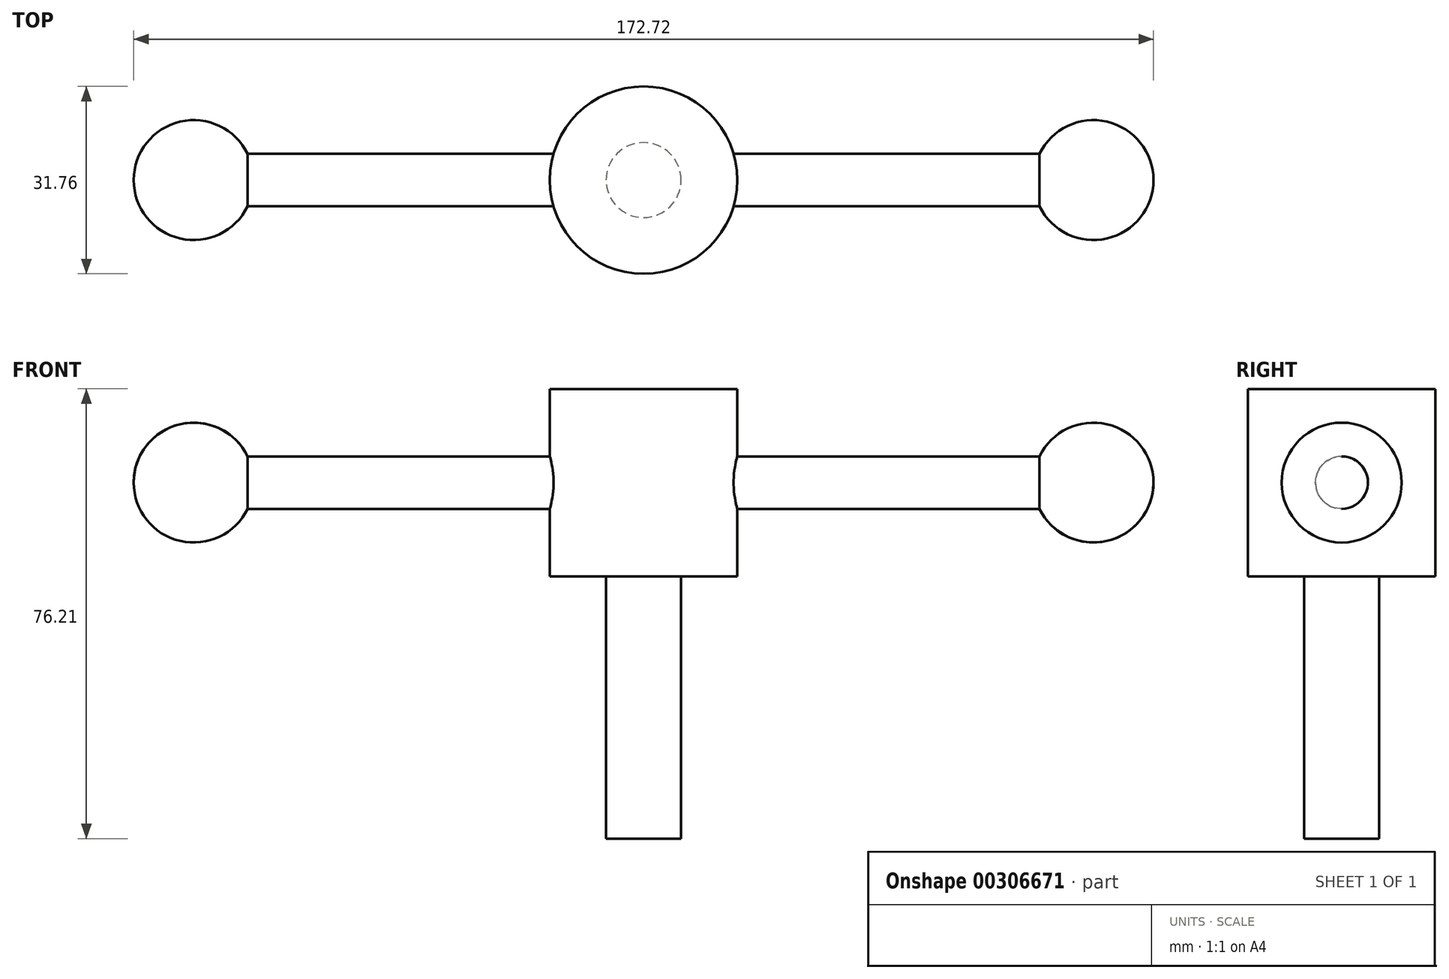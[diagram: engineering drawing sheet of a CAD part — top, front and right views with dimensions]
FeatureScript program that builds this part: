
annotation { "Feature Type Name" : "Feature", "Feature Type Description" : "" }
export const myFeature = defineFeature(function(context is Context, id is Id, definition is map)
    precondition{}
    {
        {
            var Q0;
            Q0=qCreatedBy(makeId("Top.planeOp"),FACE);
            var sketch = newSketch(context, id + "F0", { "sketchPlane" : qUnion([Q0])});
            skCircle(sketch, "E0", {"center": v(0, 0) * mm, "radius": 15.88 * mm});
            skSolve(sketch);
        }
        {
            var Q0;
            Q0=makeQuery(id+"F0.imprint","IMPRINT",FACE,{"disambiguationData":[TD([[makeQuery(id+"F0.imprint","IMPRINT",EDGE,{"derivedFrom":sQuery(id+"F0.wireOp",EDGE,"E0")}),1.0]])]});
            extrude(context, id + "F1", {"entities" : qUnion([Q0]), "endBound" : BoundingType.SYMMETRIC, "depth" : 31.75 * mm});
        }
        {
            var Q0;
            Q0=makeQuery(id+"F1.opExtrude","CAP_FACE",FACE,{"disambiguationData":[OSD([sQuery(id+"F0.wireOp",EDGE,"E0")])],"isStart":true});
            var sketch = newSketch(context, id + "F2", { "sketchPlane" : qUnion([Q0])});
            skCircle(sketch, "E1", {"center": v(0, 0) * mm, "radius": 6.35 * mm});
            skSolve(sketch);
        }
        {
            var Q0;
            Q0=makeQuery(id+"F2.imprint","IMPRINT",FACE,{"disambiguationData":[TD([[makeQuery(id+"F2.imprint","IMPRINT",EDGE,{"derivedFrom":sQuery(id+"F2.wireOp",EDGE,"E1")}),1.0]])]});
            extrude(context, id + "F3", {"entities" : qUnion([Q0]), "operationType" : NewBodyOperationType.ADD, "depth" : 44.45 * mm});
        }
        {
            var Q0;
            Q0=qCreatedBy(makeId("Right.planeOp"),FACE);
            var sketch = newSketch(context, id + "F4", { "sketchPlane" : qUnion([Q0])});
            skCircle(sketch, "E2", {"center": v(0, 0) * mm, "radius": 4.45 * mm});
            skSolve(sketch);
        }
        {
            var Q0;
            Q0 = qSketchRegion(id + "F4", true);
            extrude(context, id + "F5", {"entities" : qUnion([Q0]), "operationType" : NewBodyOperationType.ADD, "endBound" : BoundingType.SYMMETRIC, "depth" : 152.4 * mm});
        }
        {
            var Q0;
            Q0=qCreatedBy(makeId("Front.planeOp"),FACE);
            var sketch = newSketch(context, id + "F6", { "sketchPlane" : qUnion([Q0])});
            skLineSegment(sketch, "E3.0", {"start": v(-76.2, 4.45) * mm, "end": v(-76.2, -4.45) * mm});
            skLineSegment(sketch, "E4.0", {"start": v(76.2, 4.45) * mm, "end": v(76.2, -4.45) * mm});
            skArc(sketch, "E5", {"start": v(-67.06, 4.45) * mm, "mid": v(-78.48, 9.9) * mm, "end": v(-86.36, 0) * mm});
            skArc(sketch, "E6", {"start": v(86.36, 0) * mm, "mid": v(78.48, 9.9) * mm, "end": v(67.06, 4.45) * mm});
            skLineSegment(sketch, "E7", {"start": v(-76.2, 0) * mm, "end": v(-86.36, 0) * mm});
            skLineSegment(sketch, "E8", {"start": v(76.2, 0) * mm, "end": v(86.36, 0) * mm});
            skLineSegment(sketch, "E9", {"start": v(-76.2, 0) * mm, "end": v(-76.2, 4.45) * mm});
            skLineSegment(sketch, "E10", {"start": v(76.2, 0) * mm, "end": v(76.2, 4.45) * mm});
            skLineSegment(sketch, "E11", {"start": v(76.2, 4.45) * mm, "end": v(67.06, 4.45) * mm});
            skLineSegment(sketch, "E12", {"start": v(-76.2, 4.45) * mm, "end": v(-67.06, 4.45) * mm});
            skLineSegment(sketch, "E13", {"start": v(0, 0) * mm, "end": v(-13.53, 0) * mm, "construction": true});
            skSolve(sketch);
        }
        {
            var Q0;
            Q0=makeQuery(id+"F6.imprint","IMPRINT",FACE,{"disambiguationData":[TD([[makeQuery(id+"F6.imprint","IMPRINT",EDGE,{"derivedFrom":sQuery(id+"F6.wireOp",EDGE,"E5")}),1.0]])]});
            var Q1;
            Q1=makeQuery(id+"F6.imprint","IMPRINT",FACE,{"disambiguationData":[TD([[makeQuery(id+"F6.imprint","IMPRINT",EDGE,{"derivedFrom":sQuery(id+"F6.wireOp",EDGE,"E6")}),1.0]])]});
            var Q2;
            Q2=sQuery(id+"F6.wireOp",EDGE,"E13");
            revolve(context, id + "F7", {"operationType" : NewBodyOperationType.ADD, "entities" : qUnion([Q0, Q1]), "axis" : qUnion([Q2]), "revolveType" : RevolveType.FULL});
        }
    });
